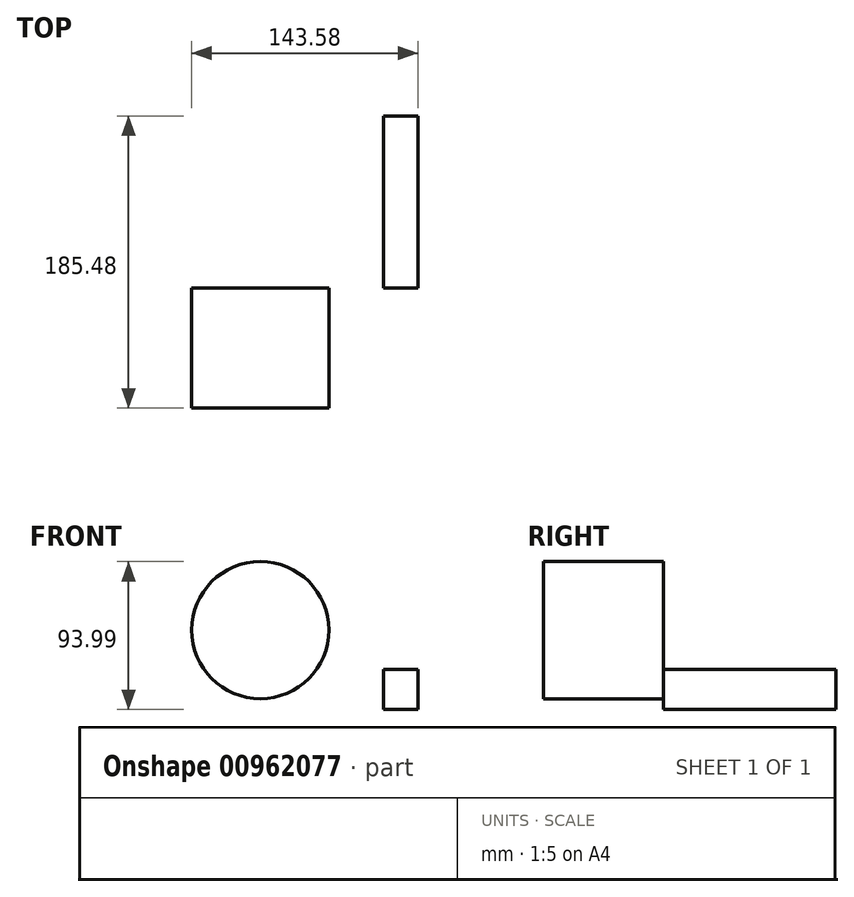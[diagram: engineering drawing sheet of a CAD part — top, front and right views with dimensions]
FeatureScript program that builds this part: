
annotation { "Feature Type Name" : "Feature", "Feature Type Description" : "" }
export const myFeature = defineFeature(function(context is Context, id is Id, definition is map)
    precondition{}
    {
        {
            var Q0;
            Q0=qCreatedBy(makeId("Top.planeOp"),FACE);
            var sketch = newSketch(context, id + "F0", { "sketchPlane" : qUnion([Q0])});
            skLineSegment(sketch, "E0.bottom", {"start": v(16.28, 109.28) * mm, "end": v(38, 109.28) * mm});
            skLineSegment(sketch, "E0.top", {"start": v(16.28, 0) * mm, "end": v(38, 0) * mm});
            skLineSegment(sketch, "E0.left", {"start": v(16.28, 109.28) * mm, "end": v(16.28, 0) * mm});
            skLineSegment(sketch, "E0.right", {"start": v(38, 109.28) * mm, "end": v(38, 0) * mm});
            skSolve(sketch);
        }
        {
            var Q0;
            Q0=makeQuery(id+"F0.imprint","IMPRINT",FACE,{"disambiguationData":[TD([[makeQuery(id+"F0.imprint","IMPRINT",EDGE,{"derivedFrom":sQuery(id+"F0.wireOp",EDGE,"E0.bottom")}),-1.0]])]});
            extrude(context, id + "F1", {"entities" : qUnion([Q0]), "depth" : 25.4 * mm, "offsetDistance" : 25.4 * mm});
        }
        {
            var Q0;
            Q0=qCreatedBy(makeId("Front.planeOp"),FACE);
            var sketch = newSketch(context, id + "F2", { "sketchPlane" : qUnion([Q0])});
            skCircle(sketch, "E1", {"center": v(-62, 50.4) * mm, "radius": 43.58 * mm});
            skSolve(sketch);
        }
        {
            var Q0;
            Q0=makeQuery(id+"F2.imprint","IMPRINT",FACE,{"disambiguationData":[TD([[makeQuery(id+"F2.imprint","IMPRINT",EDGE,{"derivedFrom":sQuery(id+"F2.wireOp",EDGE,"E1")}),1.0]])]});
            extrude(context, id + "F3", {"entities" : qUnion([Q0]), "depth" : 76.2 * mm, "offsetDistance" : 25.4 * mm});
        }
    });
